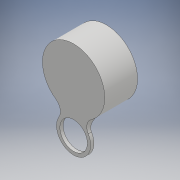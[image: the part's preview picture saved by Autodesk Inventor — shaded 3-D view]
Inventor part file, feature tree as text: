
AUTODESK INVENTOR PART (.ipt)
format: ipt  version: 2018 (Build 220112000, 112)  size: 154,624 bytes
history: native  units: mm
features: extrude x4, sketch x4, fillet x2
ambient origin geometry x8: Origin, YZ Plane, XZ Plane, XY Plane, X Axis, Y Axis, Z Axis, Center Point
bodies: Solid1 (feature_tree)
feature tree (10):
  extrude  "Extrusion1"  Depth=0.635mm TaperAngle=0.0deg
  extrude  "Extrusion2"  Depth=5.715mm TaperAngle=0.0deg
  extrude  "Extrusion3"  Depth=3.302mm
  extrude  "Extrusion4"  Depth=2.0mm TaperAngle=0.0deg
  fillet  "Fillet1"  Radius=0.635mm
  fillet  "Fillet2"  Radius=2.0mm
  sketch  "Sketch1"  dims[d0=12.065mm d1=0.635mm d2=0.0mm]
  sketch  "Sketch2"  dims[d3=10.795mm d4=5.715mm d5=0.0mm]
  sketch  "Sketch3"  dims[d6=3.302mm d7=6.604mm]
  sketch  "Sketch4"  dims[d8=5.334mm d9=0.635mm d10=0.0mm d11=0.635mm d12=0.0mm d13=2.0mm d14=2.0mm]
